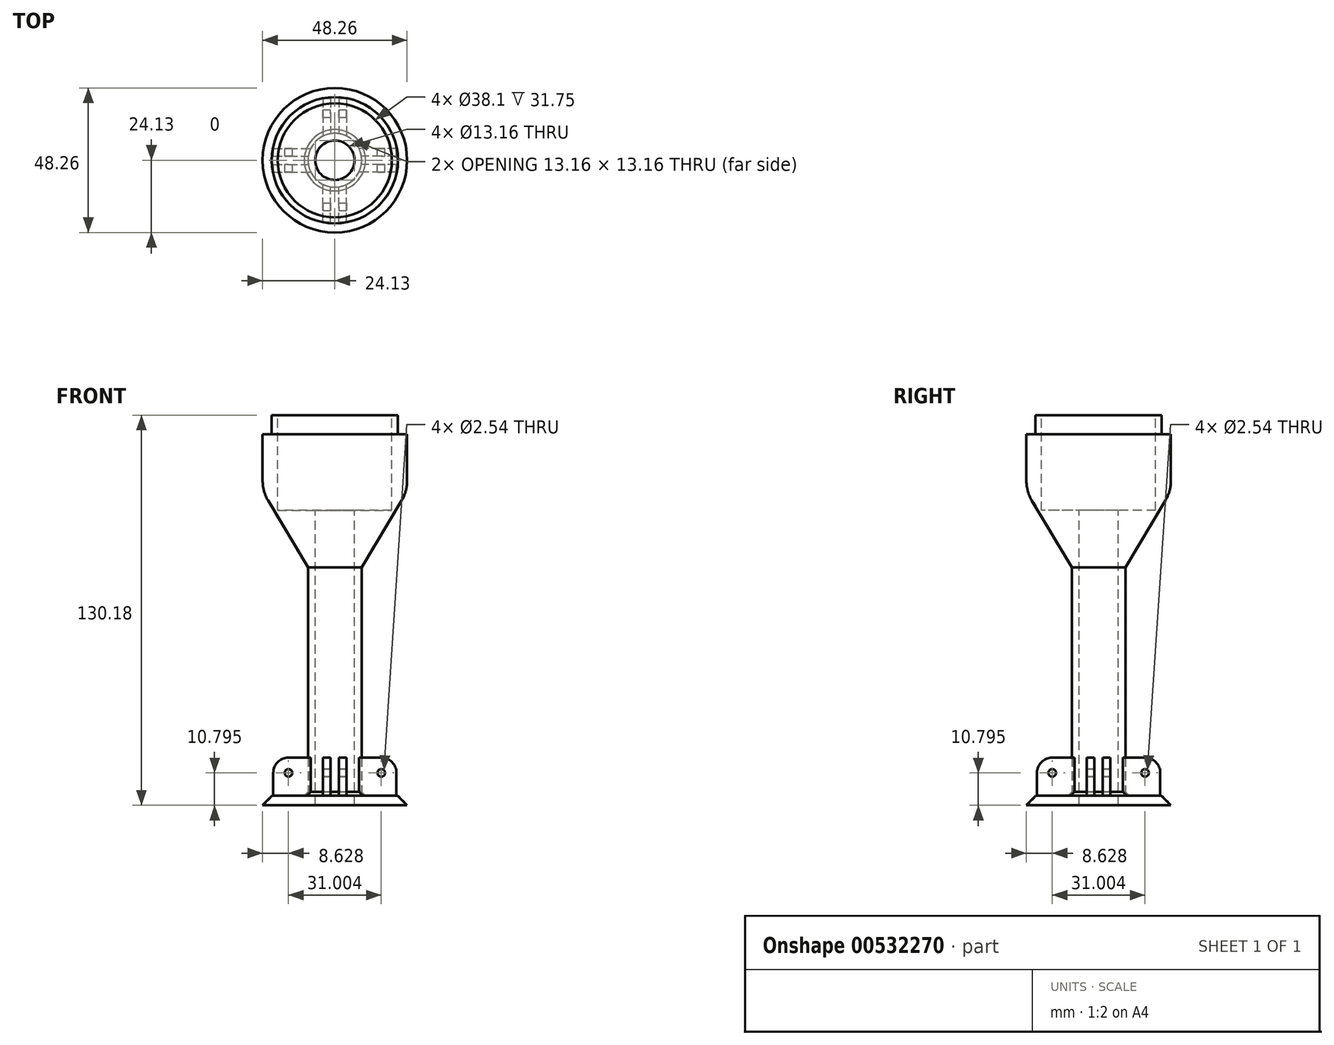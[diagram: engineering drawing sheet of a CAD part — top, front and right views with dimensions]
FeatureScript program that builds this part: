
annotation { "Feature Type Name" : "Feature", "Feature Type Description" : "" }
export const myFeature = defineFeature(function(context is Context, id is Id, definition is map)
    precondition{}
    {
        {
            var Q0;
            Q0=qCreatedBy(makeId("Front.planeOp"),FACE);
            var sketch = newSketch(context, id + "F0", { "sketchPlane" : qUnion([Q0])});
            skLineSegment(sketch, "E0.bottom", {"start": v(0, 0) * mm, "end": v(24.13, 0) * mm});
            skLineSegment(sketch, "E0.top", {"start": v(0, 130.18) * mm, "end": v(24.13, 130.18) * mm});
            skLineSegment(sketch, "E0.left", {"start": v(0, 0) * mm, "end": v(0, 130.17) * mm});
            skLineSegment(sketch, "E0.right", {"start": v(24.13, 0) * mm, "end": v(24.13, 3.18) * mm});
            skLineSegment(sketch, "E1", {"start": v(22.33, 101.77) * mm, "end": v(8.97, 79.38) * mm});
            skLineSegment(sketch, "E2", {"start": v(8.97, 79.38) * mm, "end": v(8.97, 3.18) * mm});
            skLineSegment(sketch, "E3", {"start": v(8.97, 3.17) * mm, "end": v(24.13, 3.18) * mm});
            skLineSegment(sketch, "E4.trimOffspring", {"start": v(24.13, 108.28) * mm, "end": v(24.13, 130.17) * mm});
            skPoint(sketch, "E5.visualSharp", {"position": v(24.13, 104.77) * mm});
            skArc(sketch, "E5.filletArc", {"start": v(22.33, 101.77) * mm, "mid": v(23.67, 104.9) * mm, "end": v(24.13, 108.28) * mm});
            skSolve(sketch);
        }
        {
            var Q0;
            Q0=makeQuery(id+"F0.imprint","IMPRINT",FACE,{"disambiguationData":[TD([[makeQuery(id+"F0.imprint","IMPRINT",EDGE,{"derivedFrom":sQuery(id+"F0.wireOp",EDGE,"E0.bottom")}),1.0]])]});
            var Q1;
            Q1=sQuery(id+"F0.wireOp",EDGE,"E0.left");
            revolve(context, id + "F1", {"entities" : qUnion([Q0]), "axis" : qUnion([Q1]), "revolveType" : RevolveType.FULL});
        }
        {
            var Q0;
            Q0=qCreatedBy(makeId("Front.planeOp"),FACE);
            var sketch = newSketch(context, id + "F2", { "sketchPlane" : qUnion([Q0])});
            skLineSegment(sketch, "E6.bottom", {"start": v(26.16, 123.82) * mm, "end": v(21.08, 123.82) * mm});
            skLineSegment(sketch, "E6.top", {"start": v(26.16, 131.44) * mm, "end": v(21.08, 131.44) * mm});
            skLineSegment(sketch, "E6.left", {"start": v(26.16, 123.82) * mm, "end": v(26.16, 131.44) * mm});
            skLineSegment(sketch, "E6.right", {"start": v(21.08, 123.82) * mm, "end": v(21.08, 131.44) * mm});
            skSolve(sketch);
        }
        {
            var Q0;
            Q0=makeQuery(id+"F2.imprint","IMPRINT",FACE,{"disambiguationData":[TD([[makeQuery(id+"F2.imprint","IMPRINT",EDGE,{"derivedFrom":sQuery(id+"F2.wireOp",EDGE,"E6.bottom")}),-1.0]])]});
            var Q1;
            Q1=makeQuery(id+"F1.opRevolve","SWEPT_FACE",FACE,{"disambiguationData":[OSD([sQuery(id+"F0.wireOp",EDGE,"E2")])]});
            revolve(context, id + "F3", {"operationType" : NewBodyOperationType.REMOVE, "entities" : qUnion([Q0]), "axis" : qUnion([Q1]), "revolveType" : RevolveType.FULL, "oppositeDirection" : true});
        }
        {
            var Q0;
            Q0=makeQuery(id+"F1.opRevolve","SWEPT_FACE",FACE,{"disambiguationData":[OSD([sQuery(id+"F0.wireOp",EDGE,"E0.top")])]});
            var sketch = newSketch(context, id + "F4", { "sketchPlane" : qUnion([Q0])});
            skCircle(sketch, "E7", {"center": v(0, 0) * mm, "radius": 19.05 * mm});
            skSolve(sketch);
        }
        {
            var Q0;
            Q0=makeQuery(id+"F4.imprint","IMPRINT",FACE,{"disambiguationData":[TD([[makeQuery(id+"F4.imprint","IMPRINT",EDGE,{"derivedFrom":sQuery(id+"F4.wireOp",EDGE,"E7")}),1.0]])]});
            extrude(context, id + "F5", {"entities" : qUnion([Q0]), "operationType" : NewBodyOperationType.REMOVE, "oppositeDirection" : true, "depth" : 31.75 * mm, "offsetDistance" : 25.4 * mm});
        }
        {
            var Q0;
            Q0=makeQuery(id+"F5.boolean.opBoolean","COPY",FACE,{"derivedFrom":makeQuery(id+"F5.opExtrude","CAP_FACE",FACE,{"disambiguationData":[OSD([sQuery(id+"F4.wireOp",EDGE,"E7")])],"isStart":false})});
            var sketch = newSketch(context, id + "F6", { "sketchPlane" : qUnion([Q0])});
            skCircle(sketch, "E8", {"center": v(0, 0) * mm, "radius": 6.58 * mm});
            skSolve(sketch);
        }
        {
            var Q0;
            Q0=makeQuery(id+"F6.imprint","IMPRINT",FACE,{"disambiguationData":[TD([[makeQuery(id+"F6.imprint","IMPRINT",EDGE,{"derivedFrom":sQuery(id+"F6.wireOp",EDGE,"E8")}),1.0]])]});
            extrude(context, id + "F7", {"entities" : qUnion([Q0]), "operationType" : NewBodyOperationType.REMOVE, "endBound" : BoundingType.THROUGH_ALL, "oppositeDirection" : true, "depth" : 25.4 * mm, "offsetDistance" : 25.4 * mm});
        }
        {
            var Q0;
            Q0=makeQuery(id+"F1.opRevolve","SWEPT_EDGE",EDGE,{"disambiguationData":[OSD([sQuery(id+"F0.wireOp",EDGE,"E2"),sQuery(id+"F0.wireOp",EDGE,"E3")])]});
            chamfer(context, id + "F8", {"entities" : qUnion([Q0]), "width" : 1.27 * mm, "tangentPropagation" : true});
        }
        {
            var Q0;
            Q0=makeQuery(id+"F1.opRevolve","SWEPT_EDGE",EDGE,{"disambiguationData":[OSD([sQuery(id+"F0.wireOp",EDGE,"E0.right"),sQuery(id+"F0.wireOp",EDGE,"E3")])]});
            chamfer(context, id + "F9", {"entities" : qUnion([Q0]), "width" : 3.17 * mm, "tangentPropagation" : true});
        }
        {
            var Q0;
            Q0=makeQuery(id+"F1.opRevolve","SWEPT_FACE",FACE,{"disambiguationData":[OSD([sQuery(id+"F0.wireOp",EDGE,"E3")])]});
            var sketch = newSketch(context, id + "F10", { "sketchPlane" : qUnion([Q0])});
            skLineSegment(sketch, "E9.bottom", {"start": v(-3.94, -20.58) * mm, "end": v(-1.4, -20.58) * mm});
            skLineSegment(sketch, "E9.left", {"start": v(-3.94, -20.58) * mm, "end": v(-3.94, -5.27) * mm});
            skLineSegment(sketch, "E9.right", {"start": v(3.94, -20.58) * mm, "end": v(3.94, -5.27) * mm});
            skLineSegment(sketch, "E10.left", {"start": v(-1.4, -20.58) * mm, "end": v(-1.4, -6.43) * mm});
            skLineSegment(sketch, "E10.right", {"start": v(1.4, -20.58) * mm, "end": v(1.4, -6.43) * mm});
            skLineSegment(sketch, "E11.trimOffspring", {"start": v(1.4, -20.58) * mm, "end": v(3.94, -20.58) * mm});
            skArc(sketch, "E12", {"start": v(-3.94, -5.27) * mm, "mid": v(-2.73, -5.99) * mm, "end": v(-1.4, -6.43) * mm});
            skArc(sketch, "E13.trimOffspring", {"start": v(1.4, -6.43) * mm, "mid": v(2.73, -5.99) * mm, "end": v(3.94, -5.27) * mm});
            skSolve(sketch);
        }
        {
            var Q0;
            Q0 = qSketchRegion(id + "F10", true);
            extrude(context, id + "F11", {"entities" : qUnion([Q0]), "operationType" : NewBodyOperationType.ADD, "depth" : 12.7 * mm, "offsetDistance" : 25.4 * mm});
        }
        {
            var Q0;
            Q0=makeQuery(id+"F11.opExtrude","CAP_EDGE",EDGE,{"disambiguationData":[OSD([sQuery(id+"F10.wireOp",EDGE,"E9.bottom")])],"isStart":false});
            var Q1;
            Q1=makeQuery(id+"F11.opExtrude","CAP_EDGE",EDGE,{"disambiguationData":[OSD([sQuery(id+"F10.wireOp",EDGE,"E11.trimOffspring")])],"isStart":false});
            fillet(context, id + "F12", {"entities" : qUnion([Q0, Q1]), "radius" : 5.08 * mm, "tangentPropagation" : true, "allowEdgeOverflow" : false});
        }
        {
            var Q0;
            Q0=makeQuery(id+"F11.opExtrude","SWEPT_FACE",FACE,{"disambiguationData":[OSD([sQuery(id+"F10.wireOp",EDGE,"E9.right")])]});
            var sketch = newSketch(context, id + "F13", { "sketchPlane" : qUnion([Q0])});
            skCircle(sketch, "E14", {"center": v(-15.5, 10.8) * mm, "radius": 1.27 * mm});
            skSolve(sketch);
        }
        {
            var Q0;
            Q0=makeQuery(id+"F13.imprint","IMPRINT",FACE,{"disambiguationData":[TD([[makeQuery(id+"F13.imprint","IMPRINT",EDGE,{"derivedFrom":sQuery(id+"F13.wireOp",EDGE,"E14")}),1.0]])]});
            extrude(context, id + "F14", {"entities" : qUnion([Q0]), "operationType" : NewBodyOperationType.REMOVE, "endBound" : BoundingType.THROUGH_ALL, "oppositeDirection" : true, "depth" : 25.4 * mm, "offsetDistance" : 25.4 * mm});
        }
        {
            var Q0;
            Q0=makeQuery(id+"F1.opRevolve","SWEPT_BODY",BODY,{"disambiguationData":[OSD([sQuery(id+"F0.wireOp",EDGE,"E0.bottom"),sQuery(id+"F0.wireOp",EDGE,"E0.top"),sQuery(id+"F0.wireOp",EDGE,"E0.left"),sQuery(id+"F0.wireOp",EDGE,"E0.right"),sQuery(id+"F0.wireOp",EDGE,"E1"),sQuery(id+"F0.wireOp",EDGE,"E2"),sQuery(id+"F0.wireOp",EDGE,"E3"),sQuery(id+"F0.wireOp",EDGE,"E4.trimOffspring"),sQuery(id+"F0.wireOp",EDGE,"E5.filletArc")])]});
            var Q1;
            Q1=makeQuery(id+"F1.opRevolve","SWEPT_FACE",FACE,{"disambiguationData":[OSD([sQuery(id+"F0.wireOp",EDGE,"E2")])]});
            circularPattern(context, id + "F15", {"entities" : qUnion([Q0]), "axis" : qUnion([Q1]), "angle" : 360 * degree, "instanceCount" : 4, "equalSpace" : true});
        }
        {
            var Q0;
            Q0=makeQuery(id+"F1.opRevolve","SWEPT_FACE",FACE,{"disambiguationData":[OSD([sQuery(id+"F0.wireOp",EDGE,"E0.bottom")])]});
            var sketch = newSketch(context, id + "F16", { "sketchPlane" : qUnion([Q0])});
            skCircle(sketch, "E15", {"center": v(0, 0) * mm, "radius": 5.08 * mm});
            skCircle(sketch, "E16", {"center": v(0, 0) * mm, "radius": 3.81 * mm});
            skSolve(sketch);
        }
        {
            var Q0;
            Q0=makeQuery(id+"F16.imprint","IMPRINT",FACE,{"disambiguationData":[TD([[makeQuery(id+"F16.imprint","IMPRINT",EDGE,{"derivedFrom":sQuery(id+"F16.wireOp",EDGE,"E15")}),1.0]])]});
            extrude(context, id + "F17", {"entities" : qUnion([Q0]), "operationType" : NewBodyOperationType.REMOVE, "oppositeDirection" : true, "depth" : 1.27 * mm, "offsetDistance" : 25.4 * mm});
        }
    });
